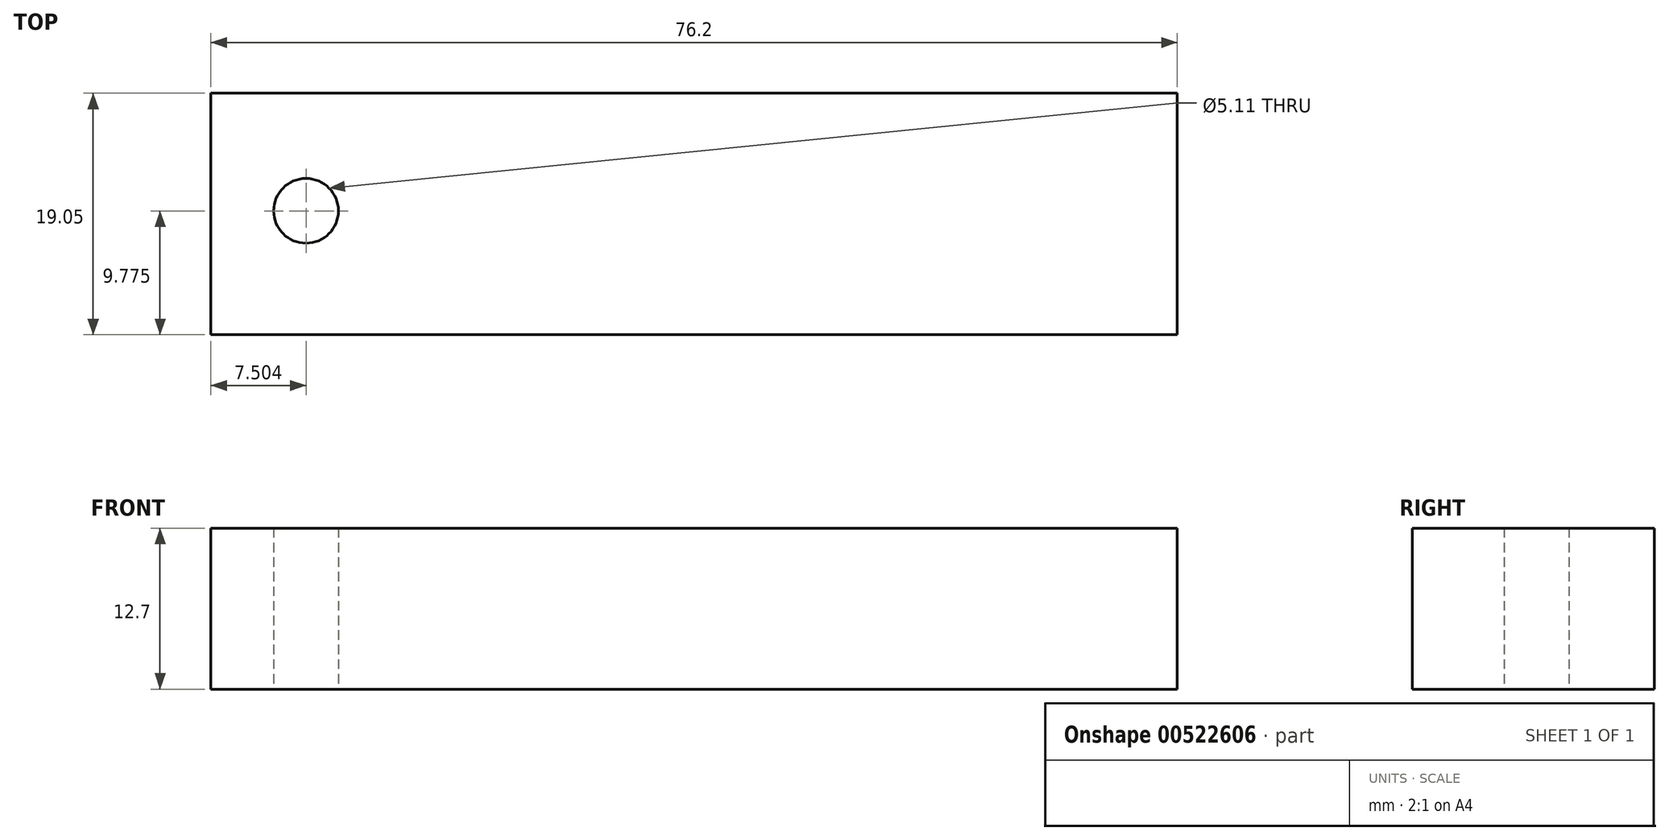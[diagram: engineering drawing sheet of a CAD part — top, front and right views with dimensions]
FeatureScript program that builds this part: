
annotation { "Feature Type Name" : "Feature", "Feature Type Description" : "" }
export const myFeature = defineFeature(function(context is Context, id is Id, definition is map)
    precondition{}
    {
        {
            var Q0;
            Q0=qCreatedBy(makeId("Top.planeOp"),FACE);
            var sketch = newSketch(context, id + "F0", { "sketchPlane" : qUnion([Q0])});
            skLineSegment(sketch, "E0", {"start": v(0, 0) * mm, "end": v(0, 19.05) * mm});
            skLineSegment(sketch, "E1", {"start": v(0, 19.05) * mm, "end": v(-76.2, 19.05) * mm});
            skLineSegment(sketch, "E2", {"start": v(-76.2, 19.05) * mm, "end": v(-76.2, 0) * mm});
            skLineSegment(sketch, "E3", {"start": v(-76.2, 0) * mm, "end": v(0, 0) * mm});
            skSolve(sketch);
        }
        {
            var Q0;
            Q0 = qSketchRegion(id + "F0", true);
            extrude(context, id + "F1", {"entities" : qUnion([Q0]), "depth" : 12.7 * mm, "offsetDistance" : 25.4 * mm});
        }
        {
            var Q0;
            Q0=qCreatedBy(makeId("Top.planeOp"),FACE);
            var sketch = newSketch(context, id + "F2", { "sketchPlane" : qUnion([Q0])});
            skPoint(sketch, "E4", {"position": v(-68.7, 9.77) * mm});
            skSolve(sketch);
        }
        {
            var Q0;
            Q0=sQuery(id+"F2.wireOp",VERTEX,"E4");
            var Q1;
            Q1=makeQuery(id+"F1.opExtrude","SWEPT_BODY",BODY,{"disambiguationData":[OSD([sQuery(id+"F0.wireOp",EDGE,"E0"),sQuery(id+"F0.wireOp",EDGE,"E1"),sQuery(id+"F0.wireOp",EDGE,"E2"),sQuery(id+"F0.wireOp",EDGE,"E3")])]});
            hole(context, id + "F3", {"style" : HoleStyle.SIMPLE, "endStyle" : HoleEndStyle.THROUGH, "oppositeDirection" : true, "standardTappedOrClearance" : lookupTablePath({ "standard" : "ANSI", "fit" : "Normal (ASME)", "size" : "#10", "type" : "Clearance" }), "standardBlindInLast" : lookupTablePath({ "fit" : "Free", "standard" : "ANSI", "size" : "#10", "type" : "Clearance" }), "holeDiameter" : 5.1 * mm, "isTappedThrough" : true, "tappedDepth" : 12.7 * mm, "tapClearance" : 3, "locations" : qUnion([Q0]), "scope" : qUnion([Q1])});
        }
    });
